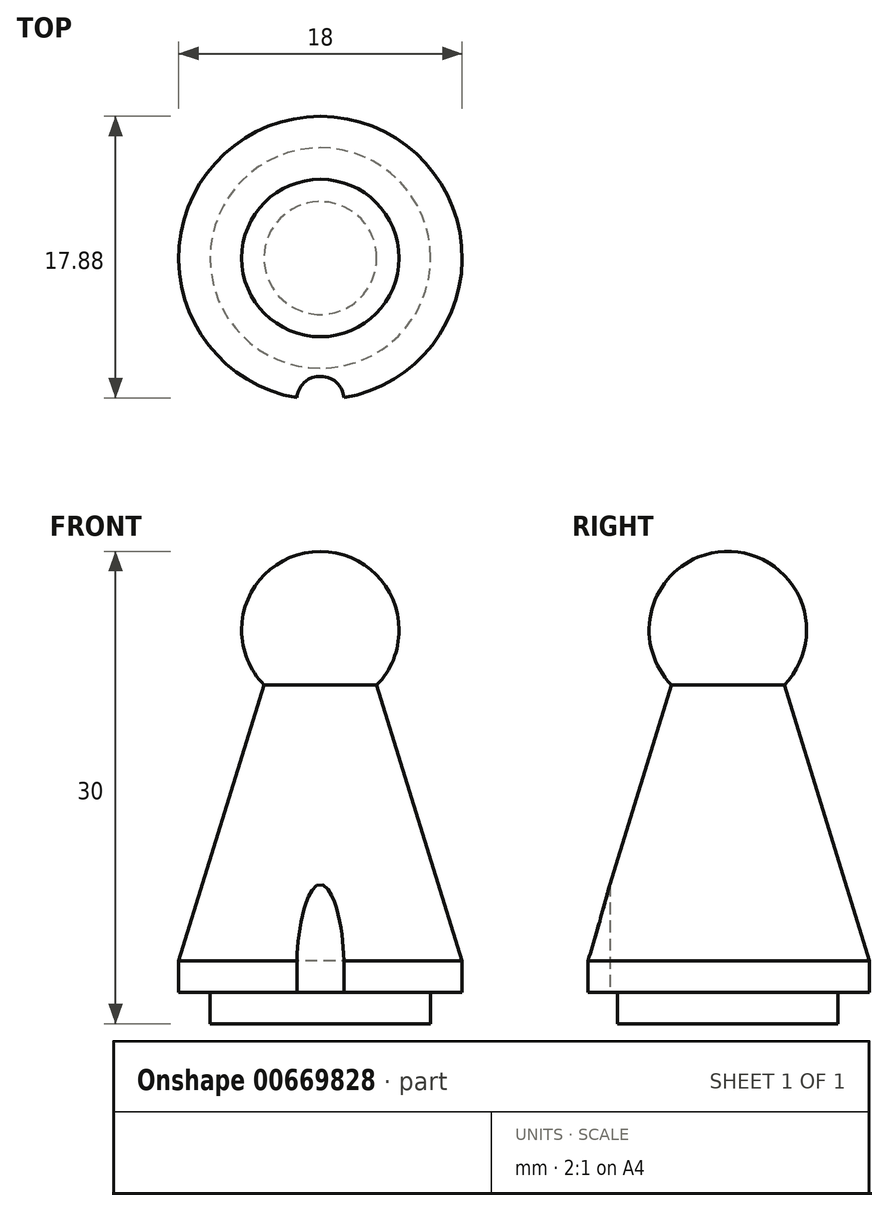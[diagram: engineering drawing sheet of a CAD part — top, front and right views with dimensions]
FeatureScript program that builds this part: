
annotation { "Feature Type Name" : "Feature", "Feature Type Description" : "" }
export const myFeature = defineFeature(function(context is Context, id is Id, definition is map)
    precondition{}
    {
        {
            var Q0;
            Q0=qCreatedBy(makeId("Top.planeOp"),FACE);
            var sketch = newSketch(context, id + "F0", { "sketchPlane" : qUnion([Q0])});
            skCircle(sketch, "E0", {"center": v(0, 0) * mm, "radius": 7 * mm});
            skSolve(sketch);
        }
        {
            var Q0;
            Q0=makeQuery(id+"F0.imprint","IMPRINT",FACE,{"disambiguationData":[TD([[makeQuery(id+"F0.imprint","IMPRINT",EDGE,{"derivedFrom":sQuery(id+"F0.wireOp",EDGE,"E0")}),1.0]])]});
            extrude(context, id + "F1", {"entities" : qUnion([Q0]), "depth" : 2 * mm, "offsetDistance" : 25 * mm});
        }
        {
            var Q0;
            Q0=makeQuery(id+"F1.opExtrude","CAP_FACE",FACE,{"disambiguationData":[OSD([sQuery(id+"F0.wireOp",EDGE,"E0")])],"isStart":false});
            var sketch = newSketch(context, id + "F2", { "sketchPlane" : qUnion([Q0])});
            skCircle(sketch, "E1", {"center": v(0, 0) * mm, "radius": 9 * mm});
            skSolve(sketch);
        }
        {
            var Q0;
            Q0=makeQuery(id+"F2.imprint","IMPRINT",FACE,{"disambiguationData":[TD([[makeQuery(id+"F2.imprint","IMPRINT",EDGE,{"derivedFrom":makeQuery(id+"F1.opExtrude","CAP_EDGE",EDGE,{"disambiguationData":[OSD([sQuery(id+"F0.wireOp",EDGE,"E0")])],"isStart":false})}),1.0]])]});
            var Q1;
            Q1=makeQuery(id+"F2.imprint","IMPRINT",FACE,{"disambiguationData":[TD([[makeQuery(id+"F2.imprint","IMPRINT",EDGE,{"derivedFrom":sQuery(id+"F2.wireOp",EDGE,"E1")}),1.0]])]});
            extrude(context, id + "F3", {"entities" : qUnion([Q0, Q1]), "operationType" : NewBodyOperationType.ADD, "depth" : 2 * mm, "offsetDistance" : 25 * mm});
        }
        {
            var Q0;
            Q0=qCreatedBy(makeId("Top.planeOp"),FACE);
            cPlane(context, id + "F4", {"entities" : qUnion([Q0]), "cplaneType" : CPlaneType.OFFSET, "offset" : 25 * mm, "width" : 150 * mm, "height" : 150 * mm});
        }
        {
            var Q0;
            Q0=qCreatedBy(id+"F4.planeOp",FACE);
            var sketch = newSketch(context, id + "F5", { "sketchPlane" : qUnion([Q0])});
            skCircle(sketch, "E2", {"center": v(0, 0) * mm, "radius": 2.5 * mm});
            skSolve(sketch);
        }
        {
            var Q1;
            Q1=makeQuery(id+"F3.opExtrude","CAP_FACE",FACE,{"disambiguationData":[OSD([sQuery(id+"F2.wireOp",EDGE,"E1")])],"isStart":false});
            var Q2;
            Q2=makeQuery(id+"F5.imprint","IMPRINT",FACE,{"disambiguationData":[TD([[makeQuery(id+"F5.imprint","IMPRINT",EDGE,{"derivedFrom":sQuery(id+"F5.wireOp",EDGE,"E2")}),1.0]])]});
            loft(context, id + "F6", {"operationType" : NewBodyOperationType.ADD, "sheetProfilesArray" : [{ "sheetProfileEntities" : qUnion([Q1]) }, { "sheetProfileEntities" : qUnion([Q2]) }]});
        }
        {
            var Q0;
            Q0=qCreatedBy(id+"F4.planeOp",FACE);
            var sketch = newSketch(context, id + "F7", { "sketchPlane" : qUnion([Q0])});
            skCircle(sketch, "E3", {"center": v(0, 0) * mm, "radius": 5 * mm});
            skLineSegment(sketch, "E4", {"start": v(-5, 0) * mm, "end": v(5, 0) * mm});
            skSolve(sketch);
        }
        {
            var Q0;
            {var subQ0=sQuery(id+"F7.wireOp",EDGE,"E4");Q0=makeQuery(id+"F7.imprint","IMPRINT",FACE,{"disambiguationData":[TD([[makeQuery(id+"F7.imprint","IMPRINT",EDGE,{"derivedFrom":subQ0}),-1.0]])]});}
            var Q1;
            Q1=sQuery(id+"F7.wireOp",EDGE,"E4");
            revolve(context, id + "F8", {"operationType" : NewBodyOperationType.ADD, "entities" : qUnion([Q0]), "axis" : qUnion([Q1]), "revolveType" : RevolveType.FULL});
        }
        {
            var Q0;
            Q0=makeQuery(id+"F3.opExtrude","CAP_FACE",FACE,{"disambiguationData":[OSD([sQuery(id+"F2.wireOp",EDGE,"E1")])],"isStart":true});
            var sketch = newSketch(context, id + "F9", { "sketchPlane" : qUnion([Q0])});
            skCircle(sketch, "E5", {"center": v(0, 9) * mm, "radius": 1.5 * mm});
            skSolve(sketch);
        }
        {
            var Q0;
            Q0=makeQuery(id+"FfqfDsfZnUAau3G_1.1.F9.imprint","IMPRINT",FACE,{"disambiguationData":[TD([[makeQuery(id+"FfqfDsfZnUAau3G_1.1.F9.imprint","IMPRINT",EDGE,{"derivedFrom":sQuery(id+"FfqfDsfZnUAau3G_1.1.F9.wireOp",EDGE,"E5")}),1.0]])]});
            var Q1;
            Q1=makeQuery(id+"FfqfDsfZnUAau3G_1.2.F9.imprint","IMPRINT",FACE,{"disambiguationData":[TD([[makeQuery(id+"FfqfDsfZnUAau3G_1.2.F9.imprint","IMPRINT",EDGE,{"derivedFrom":sQuery(id+"FfqfDsfZnUAau3G_1.2.F9.wireOp",EDGE,"E5")}),1.0]])]});
            var Q2;
            {var subQ0=sQuery(id+"F9.wireOp",EDGE,"E5");var subQ1=makeQuery(id+"F3.opExtrude","CAP_EDGE",EDGE,{"disambiguationData":[OSD([sQuery(id+"F2.wireOp",EDGE,"E1")])],"isStart":true});var subQ2=makeQuery(id+"F9.imprint","INTERSECT",VERTEX,{"disambiguationData":[OD(0.0)],"derivedFrom":[subQ1,subQ0]});Q2=makeQuery(id+"F9.imprint","IMPRINT",FACE,{"disambiguationData":[TD([[makeQuery(id+"F9.imprint","IMPRINT",EDGE,{"disambiguationData":[TD([[subQ2,-1.0]])],"derivedFrom":subQ0}),1.0]])]});}
            var Q3;
            {var subQ0=sQuery(id+"F9.wireOp",EDGE,"E5");var subQ1=makeQuery(id+"F3.opExtrude","CAP_EDGE",EDGE,{"disambiguationData":[OSD([sQuery(id+"F2.wireOp",EDGE,"E1")])],"isStart":true});var subQ2=makeQuery(id+"F9.imprint","INTERSECT",VERTEX,{"disambiguationData":[OD(0.0)],"derivedFrom":[subQ1,subQ0]});Q3=makeQuery(id+"F9.imprint","IMPRINT",FACE,{"disambiguationData":[TD([[makeQuery(id+"F9.imprint","IMPRINT",EDGE,{"disambiguationData":[TD([[subQ2,1.0]])],"derivedFrom":subQ0}),1.0]])]});}
            extrude(context, id + "F10", {"entities" : qUnion([Q0, Q1, Q2, Q3]), "operationType" : NewBodyOperationType.REMOVE, "endBound" : BoundingType.THROUGH_ALL, "oppositeDirection" : true, "depth" : 25 * mm, "offsetDistance" : 25 * mm});
        }
    });
